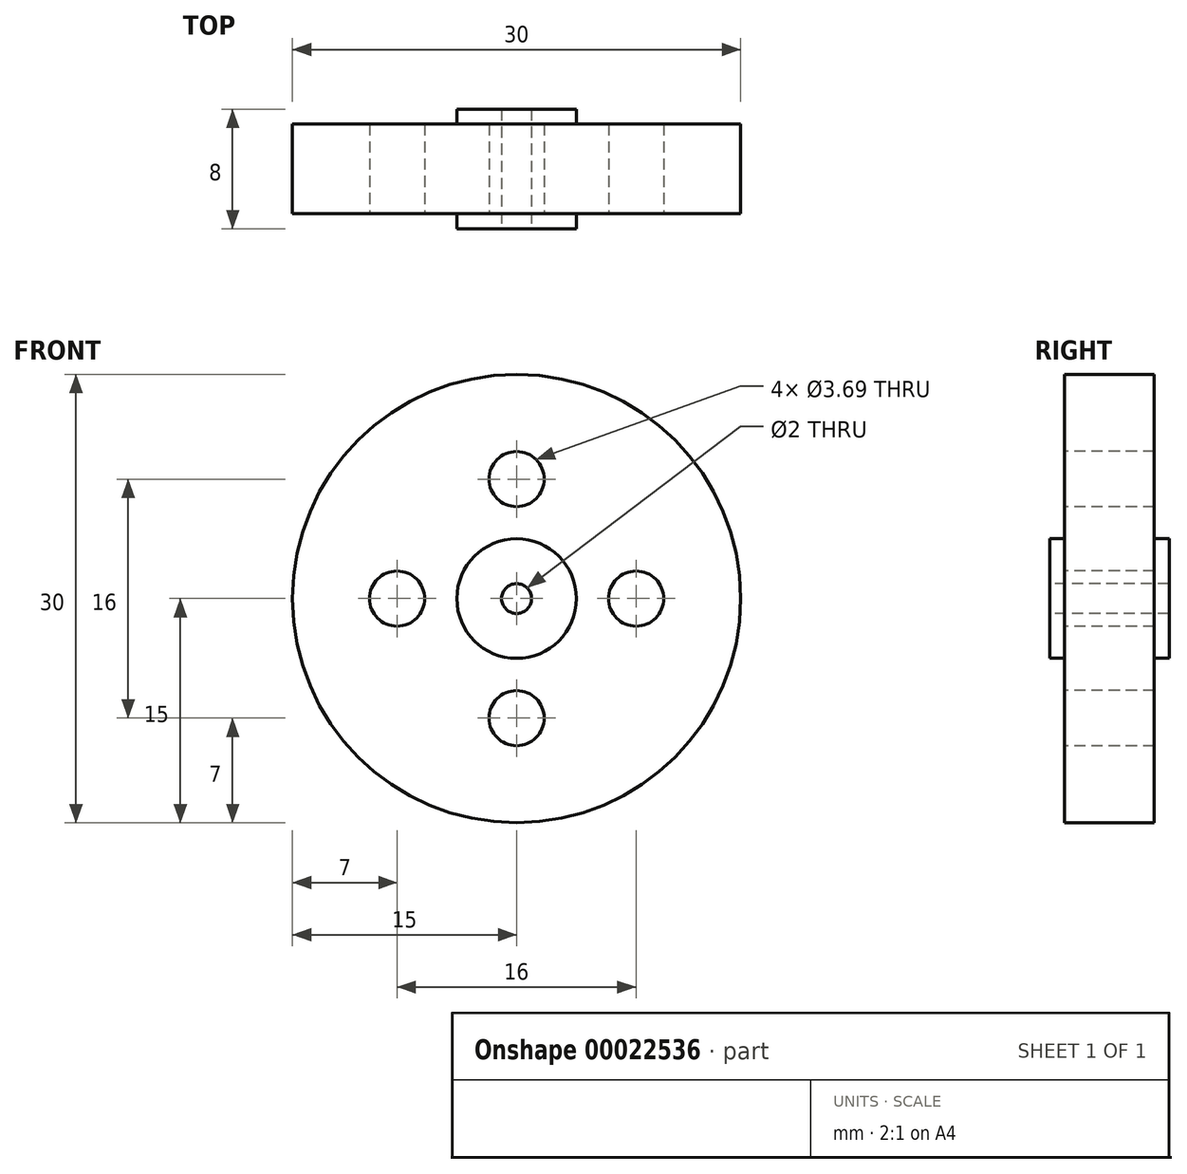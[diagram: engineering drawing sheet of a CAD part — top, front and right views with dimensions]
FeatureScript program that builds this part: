
annotation { "Feature Type Name" : "Feature", "Feature Type Description" : "" }
export const myFeature = defineFeature(function(context is Context, id is Id, definition is map)
    precondition{}
    {
        {
            var Q0;
            Q0=qCreatedBy(makeId("Front.planeOp"),FACE);
            var sketch = newSketch(context, id + "F0", { "sketchPlane" : qUnion([Q0])});
            skCircle(sketch, "E0", {"center": v(0, 0) * mm, "radius": 15 * mm});
            skSolve(sketch);
        }
        {
            var Q0;
            Q0=makeQuery(id+"F0.imprint","IMPRINT",FACE,{"disambiguationData":[TD([[makeQuery(id+"F0.imprint","IMPRINT",EDGE,{"derivedFrom":sQuery(id+"F0.wireOp",EDGE,"E0")}),1.0]])]});
            extrude(context, id + "F1", {"entities" : qUnion([Q0]), "depth" : 6 * mm});
        }
        {
            var Q0;
            Q0=makeQuery(id+"F1.opExtrude","CAP_FACE",FACE,{"disambiguationData":[OSD([sQuery(id+"F0.wireOp",EDGE,"E0")])],"isStart":false});
            var sketch = newSketch(context, id + "F2", { "sketchPlane" : qUnion([Q0])});
            skCircle(sketch, "E1", {"center": v(0, 0) * mm, "radius": 4 * mm});
            skSolve(sketch);
        }
        {
            var Q0;
            Q0=makeQuery(id+"F2.imprint","IMPRINT",FACE,{"disambiguationData":[TD([[makeQuery(id+"F2.imprint","IMPRINT",EDGE,{"derivedFrom":sQuery(id+"F2.wireOp",EDGE,"E1")}),1.0]])]});
            extrude(context, id + "F3", {"entities" : qUnion([Q0]), "operationType" : NewBodyOperationType.ADD, "depth" : 1 * mm});
        }
        {
            var Q0;
            Q0=makeQuery(id+"F3.opExtrude","CAP_FACE",FACE,{"disambiguationData":[OSD([sQuery(id+"F2.wireOp",EDGE,"E1")])],"isStart":false});
            var sketch = newSketch(context, id + "F4", { "sketchPlane" : qUnion([Q0])});
            skCircle(sketch, "E2", {"center": v(0, 0) * mm, "radius": 1 * mm});
            skSolve(sketch);
        }
        {
            var Q0;
            Q0=makeQuery(id+"F4.imprint","IMPRINT",FACE,{"disambiguationData":[TD([[makeQuery(id+"F4.imprint","IMPRINT",EDGE,{"derivedFrom":sQuery(id+"F4.wireOp",EDGE,"E2")}),1.0]])]});
            extrude(context, id + "F5", {"entities" : qUnion([Q0]), "operationType" : NewBodyOperationType.REMOVE, "oppositeDirection" : true, "depth" : 25.4 * mm});
        }
        {
            var Q0;
            Q0=makeQuery(id+"F1.opExtrude","CAP_FACE",FACE,{"disambiguationData":[OSD([sQuery(id+"F0.wireOp",EDGE,"E0")])],"isStart":true});
            var sketch = newSketch(context, id + "F6", { "sketchPlane" : qUnion([Q0])});
            skCircle(sketch, "E3", {"center": v(0, 0) * mm, "radius": 4 * mm});
            skSolve(sketch);
        }
        {
            var Q0;
            Q0=makeQuery(id+"F6.imprint","IMPRINT",FACE,{"disambiguationData":[TD([[makeQuery(id+"F6.imprint","IMPRINT",EDGE,{"derivedFrom":sQuery(id+"F6.wireOp",EDGE,"E3")}),1.0]])]});
            extrude(context, id + "F7", {"entities" : qUnion([Q0]), "operationType" : NewBodyOperationType.ADD, "depth" : 1 * mm});
        }
        {
            var Q0;
            Q0=makeQuery(id+"F1.opExtrude","CAP_FACE",FACE,{"disambiguationData":[OSD([sQuery(id+"F0.wireOp",EDGE,"E0")])],"isStart":false});
            var sketch = newSketch(context, id + "F8", { "sketchPlane" : qUnion([Q0])});
            skCircle(sketch, "E4", {"center": v(8, 0) * mm, "radius": 1.84 * mm});
            skCircle(sketch, "E5.1.0", {"center": v(0, 8) * mm, "radius": 1.84 * mm});
            skCircle(sketch, "E5.2.0", {"center": v(-8, 0) * mm, "radius": 1.84 * mm});
            skCircle(sketch, "E5.3.0", {"center": v(0, -8) * mm, "radius": 1.84 * mm});
            skPoint(sketch, "E5.center", {"position": v(0, 0) * mm});
            skSolve(sketch);
        }
        {
            var Q0;
            Q0=makeQuery(id+"F8.imprint","IMPRINT",FACE,{"disambiguationData":[TD([[makeQuery(id+"F8.imprint","IMPRINT",EDGE,{"derivedFrom":sQuery(id+"F8.wireOp",EDGE,"E5.4.0")}),1.0]])]});
            var Q1;
            Q1=makeQuery(id+"F8.imprint","IMPRINT",FACE,{"disambiguationData":[TD([[makeQuery(id+"F8.imprint","IMPRINT",EDGE,{"derivedFrom":sQuery(id+"F8.wireOp",EDGE,"E5.5.0")}),1.0]])]});
            var Q2;
            Q2=makeQuery(id+"F8.imprint","IMPRINT",FACE,{"disambiguationData":[TD([[makeQuery(id+"F8.imprint","IMPRINT",EDGE,{"derivedFrom":sQuery(id+"F8.wireOp",EDGE,"E5.3.0")}),1.0]])]});
            var Q3;
            Q3=makeQuery(id+"F8.imprint","IMPRINT",FACE,{"disambiguationData":[TD([[makeQuery(id+"F8.imprint","IMPRINT",EDGE,{"derivedFrom":sQuery(id+"F8.wireOp",EDGE,"E5.2.0")}),1.0]])]});
            var Q4;
            Q4=makeQuery(id+"F8.imprint","IMPRINT",FACE,{"disambiguationData":[TD([[makeQuery(id+"F8.imprint","IMPRINT",EDGE,{"derivedFrom":sQuery(id+"F8.wireOp",EDGE,"E5.1.0")}),1.0]])]});
            var Q5;
            Q5=makeQuery(id+"F8.imprint","IMPRINT",FACE,{"disambiguationData":[TD([[makeQuery(id+"F8.imprint","IMPRINT",EDGE,{"derivedFrom":sQuery(id+"F8.wireOp",EDGE,"E4")}),1.0]])]});
            var Q6;
            Q6=sQuery(id+"F8.wireOp",EDGE,"E5.2.0");
            var Q7;
            Q7=sQuery(id+"F8.wireOp",EDGE,"E5.3.0");
            var Q8;
            Q8=sQuery(id+"F8.wireOp",EDGE,"E5.4.0");
            var Q9;
            Q9=sQuery(id+"F8.wireOp",EDGE,"E5.5.0");
            var Q10;
            Q10=sQuery(id+"F8.wireOp",EDGE,"E4");
            var Q11;
            Q11=sQuery(id+"F8.wireOp",EDGE,"E5.1.0");
            extrude(context, id + "F9", {"entities" : qUnion([Q0, Q1, Q2, Q3, Q4, Q5]), "operationType" : NewBodyOperationType.REMOVE, "surfaceEntities" : qUnion([Q6, Q7, Q8, Q9, Q10, Q11]), "endBound" : BoundingType.THROUGH_ALL, "oppositeDirection" : true, "depth" : 25.4 * mm});
        }
        {
            var Q0;
            Q0=makeQuery(id+"F1.opExtrude","SWEPT_BODY",BODY,{"disambiguationData":[OSD([sQuery(id+"F0.wireOp",EDGE,"E0")])]});
            transform(context, id + "F10", {"entities" : qUnion([Q0]), "transformType" : TransformType.TRANSLATION_3D, "dx" : 0 * mm, "dy" : 0 * mm, "dz" : 0 * mm, "makeCopy" : true});
        }
        {
            var Q0;
            Q0=makeQuery(id+"F10.opPattern","COPY",BODY,{"derivedFrom":makeQuery(id+"F1.opExtrude","SWEPT_BODY",BODY,{"disambiguationData":[OSD([sQuery(id+"F0.wireOp",EDGE,"E0")])]}),"instanceName":"1"});
            deleteBodies(context, id + "F11", {"entities" : qUnion([Q0])});
        }
    });
